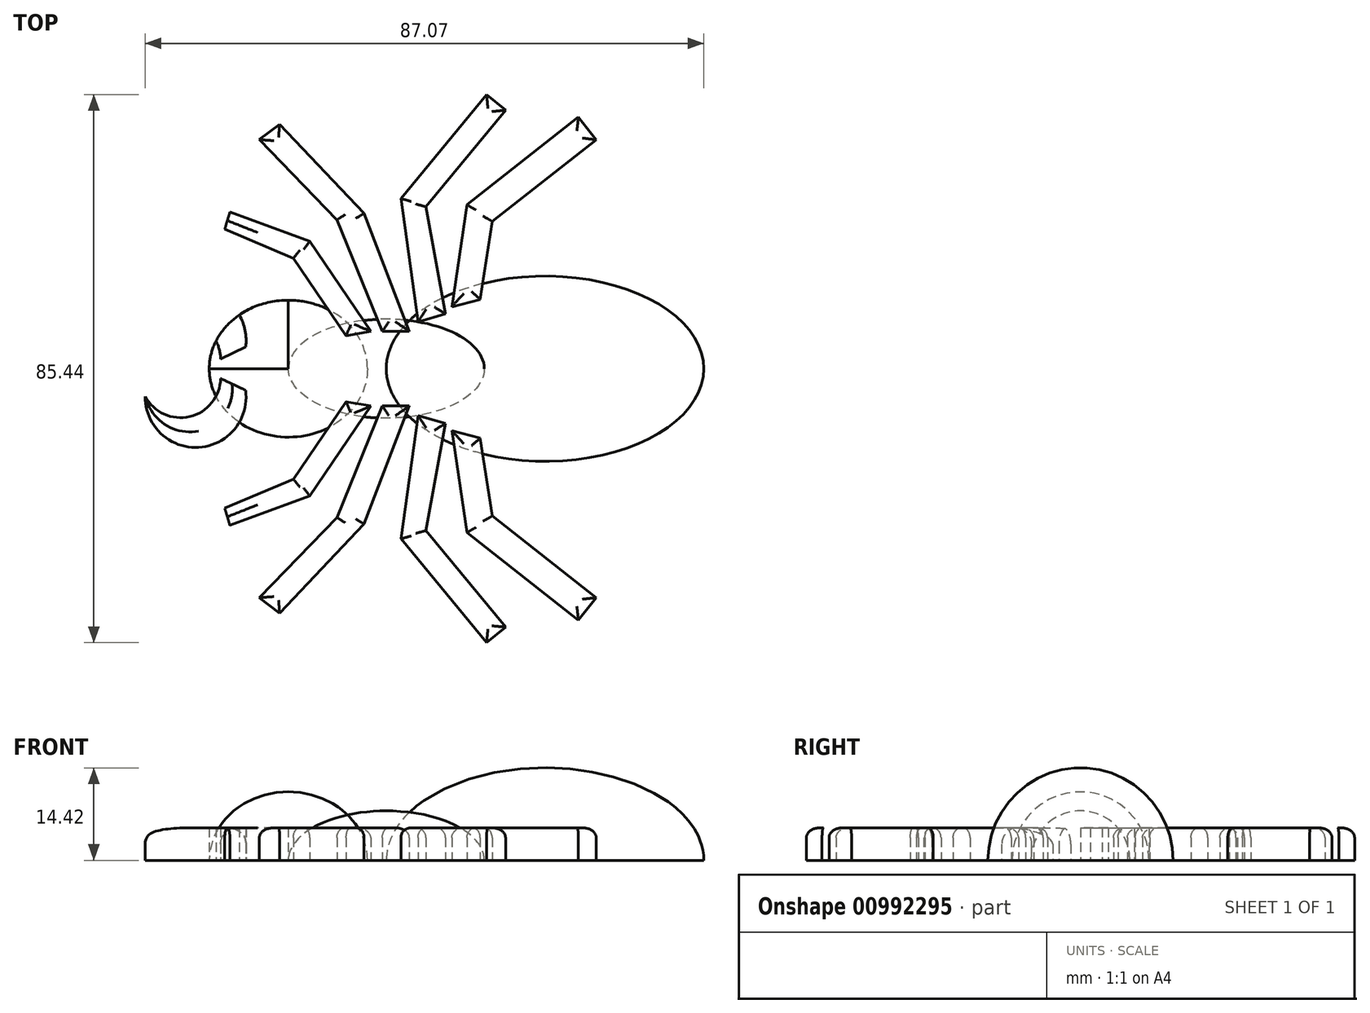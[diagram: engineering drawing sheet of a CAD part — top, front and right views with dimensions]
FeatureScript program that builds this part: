
annotation { "Feature Type Name" : "Feature", "Feature Type Description" : "" }
export const myFeature = defineFeature(function(context is Context, id is Id, definition is map)
    precondition{}
    {
        {
            var Q0;
            Q0=qCreatedBy(makeId("Top.planeOp"),FACE);
            var sketch = newSketch(context, id + "F0", { "sketchPlane" : qUnion([Q0])});
            skEllipse(sketch, "E0", {"center": v(0, 0) * mm, "majorRadius": 15.27 * mm, "minorRadius": 7.71 * mm, "majorAxis": v(1, 0)});
            skEllipse(sketch, "E1", {"center": v(24.74, 0) * mm, "majorRadius": 24.74 * mm, "minorRadius": 14.43 * mm, "majorAxis": v(-1, 0)});
            skEllipse(sketch, "E2", {"center": v(-15.27, 0) * mm, "majorRadius": 12.33 * mm, "minorRadius": 10.68 * mm, "majorAxis": v(-1, 0)});
            skLineSegment(sketch, "E3", {"start": v(-27.6, 0) * mm, "end": v(49.48, 0) * mm});
            skLineSegment(sketch, "E4", {"start": v(-15.27, -10.68) * mm, "end": v(-15.27, 10.68) * mm});
            skLineSegment(sketch, "E5", {"start": v(0, -7.71) * mm, "end": v(0, 7.71) * mm});
            skLineSegment(sketch, "E6", {"start": v(24.74, -14.43) * mm, "end": v(24.74, 14.43) * mm});
            skArc(sketch, "E7", {"start": v(-37.59, -4.31) * mm, "mid": v(-29.25, -12.26) * mm, "end": v(-21.92, -3.38) * mm});
            skArc(sketch, "E8", {"start": v(-37.59, -4.31) * mm, "mid": v(-30.62, -7.47) * mm, "end": v(-25.82, -1.52) * mm});
            skArc(sketch, "E9.MirrorCS", {"start": v(-37.59, 4.31) * mm, "mid": v(-32.07, 7.64) * mm, "end": v(-26.55, 4.31) * mm});
            skArc(sketch, "E10.MirrorCS", {"start": v(-37.59, 4.31) * mm, "mid": v(-31.82, 12) * mm, "end": v(-22.92, 8.37) * mm});
            skPoint(sketch, "E11.orphan", {"position": v(-22.92, -8.37) * mm});
            skPoint(sketch, "E12.orphan", {"position": v(-26.55, -4.31) * mm});
            skArc(sketch, "E13.MirrorCS", {"start": v(-37.59, 4.31) * mm, "mid": v(-30.62, 7.47) * mm, "end": v(-25.82, 1.52) * mm});
            skArc(sketch, "E14.MirrorCS", {"start": v(-37.59, 4.31) * mm, "mid": v(-29.25, 12.26) * mm, "end": v(-21.92, 3.38) * mm});
            skLineSegment(sketch, "E15", {"start": v(-25.82, -1.52) * mm, "end": v(-21.92, -3.38) * mm});
            skLineSegment(sketch, "E16", {"start": v(-25.82, 1.52) * mm, "end": v(-21.92, 3.38) * mm});
            skLineSegment(sketch, "E17", {"start": v(-6.26, -5.15) * mm, "end": v(-2.42, -5.82) * mm});
            skLineSegment(sketch, "E18", {"start": v(-0.62, -5.82) * mm, "end": v(3.6, -5.82) * mm});
            skLineSegment(sketch, "E19", {"start": v(4.95, -7.3) * mm, "end": v(9.23, -8.54) * mm});
            skLineSegment(sketch, "E20", {"start": v(10.2, -9.66) * mm, "end": v(14.65, -10.79) * mm});
            skLineSegment(sketch, "E21.MirrorCS", {"start": v(-6.26, 5.15) * mm, "end": v(-2.42, 5.82) * mm});
            skLineSegment(sketch, "E22.MirrorCS", {"start": v(-0.62, 5.82) * mm, "end": v(3.6, 5.82) * mm});
            skLineSegment(sketch, "E23.MirrorCS", {"start": v(4.95, 7.3) * mm, "end": v(9.23, 8.54) * mm});
            skLineSegment(sketch, "E24.MirrorCS", {"start": v(10.2, 9.66) * mm, "end": v(14.65, 10.79) * mm});
            skLineSegment(sketch, "E25", {"start": v(-6.26, -5.15) * mm, "end": v(-14.5, -17.2) * mm});
            skLineSegment(sketch, "E26", {"start": v(-2.42, -5.82) * mm, "end": v(-11.91, -19.85) * mm});
            skLineSegment(sketch, "E27", {"start": v(-11.91, -19.85) * mm, "end": v(-24.38, -24.43) * mm});
            skLineSegment(sketch, "E28", {"start": v(-14.5, -17.2) * mm, "end": v(-25.18, -21.73) * mm});
            skLineSegment(sketch, "E29", {"start": v(-25.18, -21.73) * mm, "end": v(-24.38, -24.43) * mm});
            skLineSegment(sketch, "E30", {"start": v(-0.62, -5.82) * mm, "end": v(-7.7, -23.18) * mm});
            skLineSegment(sketch, "E31", {"start": v(3.6, -5.82) * mm, "end": v(-3.46, -24.24) * mm});
            skLineSegment(sketch, "E32", {"start": v(-3.46, -24.24) * mm, "end": v(-16.63, -38.1) * mm});
            skLineSegment(sketch, "E33", {"start": v(-7.7, -23.18) * mm, "end": v(-19.8, -35.7) * mm});
            skLineSegment(sketch, "E34", {"start": v(-19.8, -35.7) * mm, "end": v(-16.63, -38.1) * mm});
            skLineSegment(sketch, "E35", {"start": v(4.95, -7.3) * mm, "end": v(2.27, -26.53) * mm});
            skLineSegment(sketch, "E36", {"start": v(2.27, -26.53) * mm, "end": v(15.63, -42.72) * mm});
            skLineSegment(sketch, "E37", {"start": v(15.63, -42.72) * mm, "end": v(18.59, -40.29) * mm});
            skLineSegment(sketch, "E38", {"start": v(18.59, -40.29) * mm, "end": v(6.18, -25.25) * mm});
            skLineSegment(sketch, "E39", {"start": v(6.18, -25.25) * mm, "end": v(9.23, -8.54) * mm});
            skLineSegment(sketch, "E40", {"start": v(10.2, -9.66) * mm, "end": v(12.57, -25.55) * mm});
            skLineSegment(sketch, "E41", {"start": v(12.57, -25.55) * mm, "end": v(29.95, -39.2) * mm});
            skLineSegment(sketch, "E42", {"start": v(29.95, -39.2) * mm, "end": v(32.7, -35.69) * mm});
            skLineSegment(sketch, "E43", {"start": v(32.7, -35.69) * mm, "end": v(16.5, -22.96) * mm});
            skLineSegment(sketch, "E44", {"start": v(16.5, -22.96) * mm, "end": v(14.65, -10.79) * mm});
            skSolve(sketch);
        }
        {
            var Q0;
            {var subQ3=sQuery(id+"F0.wireOp",EDGE,"E2");var subQ5=makeQuery(id+"F0.imprint","IMPRINT",VERTEX,{"derivedFrom":subQ3});Q0=makeQuery(id+"F0.imprint","IMPRINT",FACE,{"disambiguationData":[TD([[makeQuery(id+"F0.imprint","IMPRINT",EDGE,{"disambiguationData":[TD([[subQ5,1.0]])],"derivedFrom":subQ3}),1.0]])]});}
            var Q1;
            {var subQ3=sQuery(id+"F0.wireOp",EDGE,"E2");var subQ5=makeQuery(id+"F0.imprint","IMPRINT",VERTEX,{"derivedFrom":subQ3});Q1=makeQuery(id+"F0.imprint","IMPRINT",FACE,{"disambiguationData":[TD([[makeQuery(id+"F0.imprint","IMPRINT",EDGE,{"disambiguationData":[TD([[subQ5,1.0]])],"derivedFrom":subQ3}),-1.0]])]});}
            var Q2;
            {var subQ0=sQuery(id+"F0.wireOp",EDGE,"E5");var subQ1=sQuery(id+"F0.wireOp",EDGE,"E0");var subQ2=makeQuery(id+"F0.imprint","INTERSECT",VERTEX,{"disambiguationData":[OD(0.0)],"derivedFrom":[subQ1,subQ0]});Q2=makeQuery(id+"F0.imprint","IMPRINT",FACE,{"disambiguationData":[TD([[makeQuery(id+"F0.imprint","IMPRINT",EDGE,{"disambiguationData":[TD([[subQ2,1.0]])],"derivedFrom":subQ1}),1.0]])]});}
            var Q3;
            {var subQ4=sQuery(id+"F0.wireOp",EDGE,"E0");var subQ5=makeQuery(id+"F0.imprint","IMPRINT",VERTEX,{"derivedFrom":subQ4});Q3=makeQuery(id+"F0.imprint","IMPRINT",FACE,{"disambiguationData":[TD([[makeQuery(id+"F0.imprint","IMPRINT",EDGE,{"disambiguationData":[TD([[subQ5,1.0]])],"derivedFrom":subQ4}),1.0]])]});}
            var Q4;
            {var subQ0=sQuery(id+"F0.wireOp",EDGE,"E5");var subQ3=sQuery(id+"F0.wireOp",EDGE,"E22.MirrorCS");var subQ5=makeQuery(id+"F0.imprint","INTERSECT",VERTEX,{"derivedFrom":[subQ0,subQ3]});Q4=makeQuery(id+"F0.imprint","IMPRINT",FACE,{"disambiguationData":[TD([[makeQuery(id+"F0.imprint","IMPRINT",EDGE,{"disambiguationData":[TD([[subQ5,-1.0]])],"derivedFrom":subQ3}),-1.0]])]});}
            var Q5;
            Q5=sQuery(id+"F0.wireOp",EDGE,"E3");
            revolve(context, id + "F1", {"surfaceOperationType" : NewSurfaceOperationType.NEW, "entities" : qUnion([Q0, Q1, Q2, Q3, Q4]), "axis" : qUnion([Q5]), "revolveType" : RevolveType.ONE_DIRECTION, "angle" : 180 * degree});
        }
        {
            var Q0;
            {var subQ3=sQuery(id+"F0.wireOp",EDGE,"E0");var subQ5=makeQuery(id+"F0.imprint","IMPRINT",VERTEX,{"derivedFrom":subQ3});Q0=makeQuery(id+"F0.imprint","IMPRINT",FACE,{"disambiguationData":[TD([[makeQuery(id+"F0.imprint","IMPRINT",EDGE,{"disambiguationData":[TD([[subQ5,1.0]])],"derivedFrom":subQ3}),-1.0]])]});}
            var Q1;
            {var subQ4=sQuery(id+"F0.wireOp",EDGE,"E0");var subQ5=makeQuery(id+"F0.imprint","IMPRINT",VERTEX,{"derivedFrom":subQ4});Q1=makeQuery(id+"F0.imprint","IMPRINT",FACE,{"disambiguationData":[TD([[makeQuery(id+"F0.imprint","IMPRINT",EDGE,{"disambiguationData":[TD([[subQ5,1.0]])],"derivedFrom":subQ4}),1.0]])]});}
            var Q2;
            {var subQ0=sQuery(id+"F0.wireOp",EDGE,"E3");var subQ1=sQuery(id+"F0.wireOp",EDGE,"E1");var subQ2=makeQuery(id+"F0.imprint","INTERSECT",VERTEX,{"derivedFrom":[subQ1,subQ0]});Q2=makeQuery(id+"F0.imprint","IMPRINT",FACE,{"disambiguationData":[TD([[makeQuery(id+"F0.imprint","IMPRINT",EDGE,{"disambiguationData":[TD([[subQ2,-1.0]])],"derivedFrom":subQ1}),1.0]])]});}
            var Q3;
            Q3=sQuery(id+"F0.wireOp",EDGE,"E3");
            revolve(context, id + "F2", {"surfaceOperationType" : NewSurfaceOperationType.NEW, "entities" : qUnion([Q0, Q1, Q2]), "axis" : qUnion([Q3]), "revolveType" : RevolveType.ONE_DIRECTION, "angle" : 180 * degree});
        }
        {
            var Q0;
            {var subQ5=sQuery(id+"F0.wireOp",EDGE,"E13.MirrorCS");Q0=makeQuery(id+"F0.imprint","IMPRINT",FACE,{"disambiguationData":[TD([[makeQuery(id+"F0.imprint","IMPRINT",EDGE,{"derivedFrom":subQ5}),-1.0]])]});}
            var Q1;
            {var subQ0=sQuery(id+"F0.wireOp",EDGE,"E4");var subQ3=sQuery(id+"F0.wireOp",EDGE,"E2");var subQ5=makeQuery(id+"F0.imprint","INTERSECT",VERTEX,{"disambiguationData":[OD(1.0)],"derivedFrom":[subQ3,subQ0]});Q1=makeQuery(id+"F0.imprint","IMPRINT",FACE,{"disambiguationData":[TD([[makeQuery(id+"F0.imprint","IMPRINT",EDGE,{"disambiguationData":[TD([[subQ5,1.0]])],"derivedFrom":subQ3}),1.0]])]});}
            var Q2;
            {var subQ3=sQuery(id+"F0.wireOp",EDGE,"E2");var subQ5=makeQuery(id+"F0.imprint","IMPRINT",VERTEX,{"derivedFrom":subQ3});Q2=makeQuery(id+"F0.imprint","IMPRINT",FACE,{"disambiguationData":[TD([[makeQuery(id+"F0.imprint","IMPRINT",EDGE,{"disambiguationData":[TD([[subQ5,1.0]])],"derivedFrom":subQ3}),1.0]])]});}
            var Q3;
            {var subQ0=sQuery(id+"F0.wireOp",EDGE,"E13.MirrorCS");Q3=makeQuery(id+"F0.imprint","IMPRINT",FACE,{"disambiguationData":[TD([[makeQuery(id+"F0.imprint","IMPRINT",EDGE,{"derivedFrom":subQ0}),1.0]])]});}
            var Q4;
            Q4=sQuery(id+"F0.wireOp",EDGE,"E3");
            revolve(context, id + "F3", {"surfaceOperationType" : NewSurfaceOperationType.NEW, "entities" : qUnion([Q0, Q1, Q2, Q3]), "axis" : qUnion([Q4]), "revolveType" : RevolveType.ONE_DIRECTION, "angle" : 180 * degree});
        }
        {
            var Q0;
            {var subQ0=sQuery(id+"F0.wireOp",EDGE,"E9.MirrorCS");Q0=makeQuery(id+"F0.imprint","IMPRINT",FACE,{"disambiguationData":[TD([[makeQuery(id+"F0.imprint","IMPRINT",EDGE,{"derivedFrom":subQ0}),1.0]])]});}
            var Q1;
            {var subQ0=sQuery(id+"F0.wireOp",EDGE,"E13.MirrorCS");Q1=makeQuery(id+"F0.imprint","IMPRINT",FACE,{"disambiguationData":[TD([[makeQuery(id+"F0.imprint","IMPRINT",EDGE,{"derivedFrom":subQ0}),1.0]])]});}
            var Q2;
            {var subQ0=sQuery(id+"F0.wireOp",EDGE,"E8");var subQ1=sQuery(id+"F0.wireOp",EDGE,"E2");var subQ2=makeQuery(id+"F0.imprint","INTERSECT",VERTEX,{"derivedFrom":[subQ1,subQ0]});Q2=makeQuery(id+"F0.imprint","IMPRINT",FACE,{"disambiguationData":[TD([[makeQuery(id+"F0.imprint","IMPRINT",EDGE,{"disambiguationData":[TD([[subQ2,-1.0]])],"derivedFrom":subQ1}),-1.0]])]});}
            var Q3;
            {var subQ5=sQuery(id+"F0.wireOp",EDGE,"E15");Q3=makeQuery(id+"F0.imprint","IMPRINT",FACE,{"disambiguationData":[TD([[makeQuery(id+"F0.imprint","IMPRINT",EDGE,{"derivedFrom":subQ5}),-1.0]])]});}
            extrude(context, id + "F4", {"entities" : qUnion([Q0, Q1, Q2, Q3]), "depth" : 5.08 * mm, "offsetDistance" : 25.4 * mm});
        }
        {
            var Q0;
            Q0=makeQuery(id+"F4.opExtrude","CAP_FACE",FACE,{"disambiguationData":[OSD([sQuery(id+"F0.wireOp",EDGE,"E9.MirrorCS"),sQuery(id+"F0.wireOp",EDGE,"E10.MirrorCS"),sQuery(id+"F0.wireOp",EDGE,"E13.MirrorCS"),sQuery(id+"F0.wireOp",EDGE,"E14.MirrorCS"),sQuery(id+"F0.wireOp",EDGE,"E16")])],"isStart":false});
            var Q1;
            Q1=makeQuery(id+"F4.opExtrude","CAP_FACE",FACE,{"disambiguationData":[OSD([sQuery(id+"F0.wireOp",EDGE,"E7"),sQuery(id+"F0.wireOp",EDGE,"E8"),sQuery(id+"F0.wireOp",EDGE,"E15")])],"isStart":false});
            fillet(context, id + "F5", {"entities" : qUnion([Q0, Q1]), "radius" : 2.54 * mm, "tangentPropagation" : true, "allowEdgeOverflow" : false});
        }
        {
            var Q0;
            {var subQ0=sQuery(id+"F0.wireOp",EDGE,"E25");var subQ1=sQuery(id+"F0.wireOp",EDGE,"E0");var subQ2=makeQuery(id+"F0.imprint","INTERSECT",VERTEX,{"derivedFrom":[subQ1,subQ0]});Q0=makeQuery(id+"F0.imprint","IMPRINT",FACE,{"disambiguationData":[TD([[makeQuery(id+"F0.imprint","IMPRINT",EDGE,{"disambiguationData":[TD([[subQ2,-1.0]])],"derivedFrom":subQ1}),1.0]])]});}
            var Q1;
            {var subQ0=sQuery(id+"F0.wireOp",EDGE,"E25");var subQ1=sQuery(id+"F0.wireOp",EDGE,"E0");var subQ2=makeQuery(id+"F0.imprint","INTERSECT",VERTEX,{"derivedFrom":[subQ1,subQ0]});Q1=makeQuery(id+"F0.imprint","IMPRINT",FACE,{"disambiguationData":[TD([[makeQuery(id+"F0.imprint","IMPRINT",EDGE,{"disambiguationData":[TD([[subQ2,-1.0]])],"derivedFrom":subQ1}),-1.0]])]});}
            var Q2;
            {var subQ3=sQuery(id+"F0.wireOp",EDGE,"E27");Q2=makeQuery(id+"F0.imprint","IMPRINT",FACE,{"disambiguationData":[TD([[makeQuery(id+"F0.imprint","IMPRINT",EDGE,{"derivedFrom":subQ3}),-1.0]])]});}
            var Q3;
            {var subQ0=sQuery(id+"F0.wireOp",EDGE,"E26");var subQ1=sQuery(id+"F0.wireOp",EDGE,"E0");var subQ2=makeQuery(id+"F0.imprint","INTERSECT",VERTEX,{"derivedFrom":[subQ1,subQ0]});Q3=makeQuery(id+"F0.imprint","IMPRINT",FACE,{"disambiguationData":[TD([[makeQuery(id+"F0.imprint","IMPRINT",EDGE,{"disambiguationData":[TD([[subQ2,1.0]])],"derivedFrom":subQ1}),1.0]])]});}
            var Q4;
            {var subQ3=sQuery(id+"F0.wireOp",EDGE,"E32");Q4=makeQuery(id+"F0.imprint","IMPRINT",FACE,{"disambiguationData":[TD([[makeQuery(id+"F0.imprint","IMPRINT",EDGE,{"derivedFrom":subQ3}),-1.0]])]});}
            var Q5;
            {var subQ0=sQuery(id+"F0.wireOp",EDGE,"E30");var subQ1=sQuery(id+"F0.wireOp",EDGE,"E0");var subQ2=makeQuery(id+"F0.imprint","INTERSECT",VERTEX,{"derivedFrom":[subQ1,subQ0]});Q5=makeQuery(id+"F0.imprint","IMPRINT",FACE,{"disambiguationData":[TD([[makeQuery(id+"F0.imprint","IMPRINT",EDGE,{"disambiguationData":[TD([[subQ2,-1.0]])],"derivedFrom":subQ1}),1.0]])]});}
            var Q6;
            {var subQ5=sQuery(id+"F0.wireOp",EDGE,"E0");var subQ7=sQuery(id+"F0.wireOp",EDGE,"E31");var subQ8=makeQuery(id+"F0.imprint","INTERSECT",VERTEX,{"derivedFrom":[subQ5,subQ7]});Q6=makeQuery(id+"F0.imprint","IMPRINT",FACE,{"disambiguationData":[TD([[makeQuery(id+"F0.imprint","IMPRINT",EDGE,{"disambiguationData":[TD([[subQ8,1.0]])],"derivedFrom":subQ5}),1.0]])]});}
            var Q7;
            {var subQ0=sQuery(id+"F0.wireOp",EDGE,"E18");var subQ1=sQuery(id+"F0.wireOp",EDGE,"E1");var subQ2=makeQuery(id+"F0.imprint","INTERSECT",VERTEX,{"derivedFrom":[subQ1,subQ0]});Q7=makeQuery(id+"F0.imprint","IMPRINT",FACE,{"disambiguationData":[TD([[makeQuery(id+"F0.imprint","IMPRINT",EDGE,{"disambiguationData":[TD([[subQ2,-1.0]])],"derivedFrom":subQ1}),1.0]])]});}
            var Q8;
            {var subQ5=sQuery(id+"F0.wireOp",EDGE,"E19");Q8=makeQuery(id+"F0.imprint","IMPRINT",FACE,{"disambiguationData":[TD([[makeQuery(id+"F0.imprint","IMPRINT",EDGE,{"derivedFrom":subQ5}),-1.0]])]});}
            var Q9;
            {var subQ5=sQuery(id+"F0.wireOp",EDGE,"E20");Q9=makeQuery(id+"F0.imprint","IMPRINT",FACE,{"disambiguationData":[TD([[makeQuery(id+"F0.imprint","IMPRINT",EDGE,{"derivedFrom":subQ5}),-1.0]])]});}
            var Q10;
            {var subQ0=sQuery(id+"F0.wireOp",EDGE,"E36");Q10=makeQuery(id+"F0.imprint","IMPRINT",FACE,{"disambiguationData":[TD([[makeQuery(id+"F0.imprint","IMPRINT",EDGE,{"derivedFrom":subQ0}),1.0]])]});}
            var Q11;
            {var subQ0=sQuery(id+"F0.wireOp",EDGE,"E41");Q11=makeQuery(id+"F0.imprint","IMPRINT",FACE,{"disambiguationData":[TD([[makeQuery(id+"F0.imprint","IMPRINT",EDGE,{"derivedFrom":subQ0}),1.0]])]});}
            extrude(context, id + "F6", {"entities" : qUnion([Q0, Q1, Q2, Q3, Q4, Q5, Q6, Q7, Q8, Q9, Q10, Q11]), "depth" : 5.08 * mm, "offsetDistance" : 25.4 * mm});
        }
        {
            var Q0;
            Q0=makeQuery(id+"F6.opExtrude","CAP_FACE",FACE,{"disambiguationData":[OSD([sQuery(id+"F0.wireOp",EDGE,"E17"),sQuery(id+"F0.wireOp",EDGE,"E25"),sQuery(id+"F0.wireOp",EDGE,"E26"),sQuery(id+"F0.wireOp",EDGE,"E27"),sQuery(id+"F0.wireOp",EDGE,"E28"),sQuery(id+"F0.wireOp",EDGE,"E29")])],"isStart":false});
            var Q1;
            Q1=makeQuery(id+"F6.opExtrude","CAP_FACE",FACE,{"disambiguationData":[OSD([sQuery(id+"F0.wireOp",EDGE,"E18"),sQuery(id+"F0.wireOp",EDGE,"E30"),sQuery(id+"F0.wireOp",EDGE,"E31"),sQuery(id+"F0.wireOp",EDGE,"E32"),sQuery(id+"F0.wireOp",EDGE,"E33"),sQuery(id+"F0.wireOp",EDGE,"E34")])],"isStart":false});
            var Q2;
            Q2=makeQuery(id+"F6.opExtrude","CAP_FACE",FACE,{"disambiguationData":[OSD([sQuery(id+"F0.wireOp",EDGE,"E19"),sQuery(id+"F0.wireOp",EDGE,"E35"),sQuery(id+"F0.wireOp",EDGE,"E36"),sQuery(id+"F0.wireOp",EDGE,"E37"),sQuery(id+"F0.wireOp",EDGE,"E38"),sQuery(id+"F0.wireOp",EDGE,"E39")])],"isStart":false});
            var Q3;
            Q3=makeQuery(id+"F6.opExtrude","CAP_FACE",FACE,{"disambiguationData":[OSD([sQuery(id+"F0.wireOp",EDGE,"E20"),sQuery(id+"F0.wireOp",EDGE,"E40"),sQuery(id+"F0.wireOp",EDGE,"E41"),sQuery(id+"F0.wireOp",EDGE,"E42"),sQuery(id+"F0.wireOp",EDGE,"E43"),sQuery(id+"F0.wireOp",EDGE,"E44")])],"isStart":false});
            fillet(context, id + "F7", {"entities" : qUnion([Q0, Q1, Q2, Q3]), "radius" : 1.52 * mm, "tangentPropagation" : true, "allowEdgeOverflow" : false});
        }
        {
            var Q0;
            Q0=makeQuery(id+"F6.opExtrude","SWEPT_BODY",BODY,{"disambiguationData":[OSD([sQuery(id+"F0.wireOp",EDGE,"E17"),sQuery(id+"F0.wireOp",EDGE,"E25"),sQuery(id+"F0.wireOp",EDGE,"E26"),sQuery(id+"F0.wireOp",EDGE,"E27"),sQuery(id+"F0.wireOp",EDGE,"E28"),sQuery(id+"F0.wireOp",EDGE,"E29")])]});
            var Q1;
            Q1=makeQuery(id+"F6.opExtrude","SWEPT_BODY",BODY,{"disambiguationData":[OSD([sQuery(id+"F0.wireOp",EDGE,"E18"),sQuery(id+"F0.wireOp",EDGE,"E30"),sQuery(id+"F0.wireOp",EDGE,"E31"),sQuery(id+"F0.wireOp",EDGE,"E32"),sQuery(id+"F0.wireOp",EDGE,"E33"),sQuery(id+"F0.wireOp",EDGE,"E34")])]});
            var Q2;
            Q2=makeQuery(id+"F6.opExtrude","SWEPT_BODY",BODY,{"disambiguationData":[OSD([sQuery(id+"F0.wireOp",EDGE,"E19"),sQuery(id+"F0.wireOp",EDGE,"E35"),sQuery(id+"F0.wireOp",EDGE,"E36"),sQuery(id+"F0.wireOp",EDGE,"E37"),sQuery(id+"F0.wireOp",EDGE,"E38"),sQuery(id+"F0.wireOp",EDGE,"E39")])]});
            var Q3;
            Q3=makeQuery(id+"F6.opExtrude","SWEPT_BODY",BODY,{"disambiguationData":[OSD([sQuery(id+"F0.wireOp",EDGE,"E20"),sQuery(id+"F0.wireOp",EDGE,"E40"),sQuery(id+"F0.wireOp",EDGE,"E41"),sQuery(id+"F0.wireOp",EDGE,"E42"),sQuery(id+"F0.wireOp",EDGE,"E43"),sQuery(id+"F0.wireOp",EDGE,"E44")])]});
            var Q4;
            Q4=qCreatedBy(makeId("Front.planeOp"),FACE);
            mirror(context, id + "F8", {"entities" : qUnion([Q0, Q1, Q2, Q3]), "mirrorPlane" : qUnion([Q4])});
        }
    });
